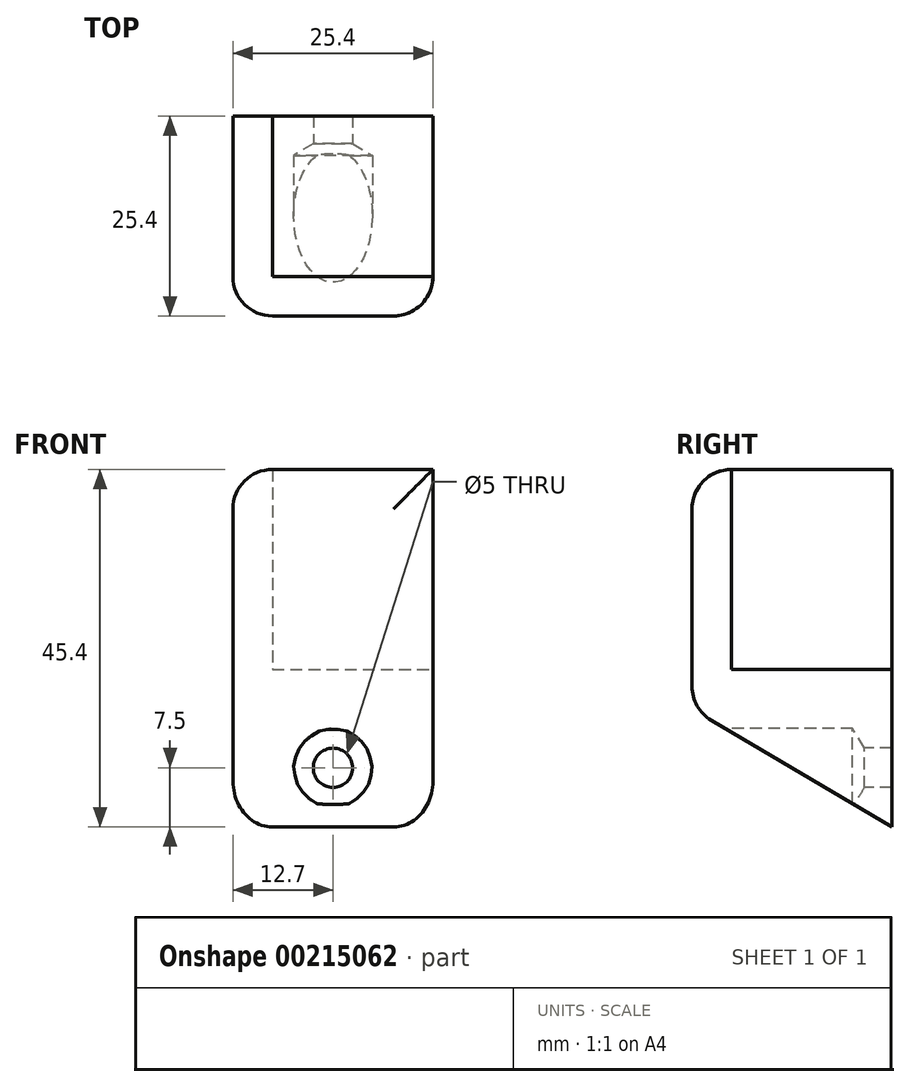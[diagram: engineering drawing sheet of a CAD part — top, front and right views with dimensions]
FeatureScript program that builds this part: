
annotation { "Feature Type Name" : "Feature", "Feature Type Description" : "" }
export const myFeature = defineFeature(function(context is Context, id is Id, definition is map)
    precondition{}
    {
        {
            var Q0;
            Q0=qCreatedBy(makeId("Top.planeOp"),FACE);
            var sketch = newSketch(context, id + "F0", { "sketchPlane" : qUnion([Q0])});
            skLineSegment(sketch, "E0.bottom", {"start": v(0, 0) * mm, "end": v(25.4, 0) * mm});
            skLineSegment(sketch, "E0.top", {"start": v(0, 25.4) * mm, "end": v(25.4, 25.4) * mm});
            skLineSegment(sketch, "E0.left", {"start": v(0, 0) * mm, "end": v(0, 25.4) * mm});
            skLineSegment(sketch, "E0.right", {"start": v(25.4, 0) * mm, "end": v(25.4, 25.4) * mm});
            skSolve(sketch);
        }
        {
            var Q0;
            Q0 = qSketchRegion(id + "F0", true);
            extrude(context, id + "F1", {"entities" : qUnion([Q0]), "depth" : 5 * mm});
        }
        {
            var Q0;
            Q0=makeQuery(id+"F1.opExtrude","CAP_FACE",FACE,{"disambiguationData":[OSD([sQuery(id+"F0.wireOp",EDGE,"E0.bottom"),sQuery(id+"F0.wireOp",EDGE,"E0.top"),sQuery(id+"F0.wireOp",EDGE,"E0.left"),sQuery(id+"F0.wireOp",EDGE,"E0.right")])],"isStart":false});
            var sketch = newSketch(context, id + "F2", { "sketchPlane" : qUnion([Q0])});
            skLineSegment(sketch, "E1", {"start": v(0, 25.4) * mm, "end": v(0, 0) * mm});
            skLineSegment(sketch, "E2", {"start": v(0, 0) * mm, "end": v(25.4, 0) * mm});
            skLineSegment(sketch, "E3", {"start": v(25.4, 0) * mm, "end": v(25.4, 5) * mm});
            skLineSegment(sketch, "E4", {"start": v(25.4, 5) * mm, "end": v(5, 5) * mm});
            skLineSegment(sketch, "E5", {"start": v(5, 5) * mm, "end": v(5, 25.4) * mm});
            skLineSegment(sketch, "E6", {"start": v(5, 25.4) * mm, "end": v(0, 25.4) * mm});
            skSolve(sketch);
        }
        {
            var Q0;
            Q0 = qSketchRegion(id + "F2", true);
            extrude(context, id + "F3", {"entities" : qUnion([Q0]), "operationType" : NewBodyOperationType.ADD, "depth" : 25.4 * mm});
        }
        {
            var Q0;
            Q0=makeQuery(id+"F3.boolean.opBoolean","MERGE",FACE,{"derivedFrom":[makeQuery(id+"F1.opExtrude","SWEPT_FACE",FACE,{"disambiguationData":[OSD([sQuery(id+"F0.wireOp",EDGE,"E0.right")])]}),makeQuery(id+"F3.opExtrude","SWEPT_FACE",FACE,{"disambiguationData":[OSD([sQuery(id+"F2.wireOp",EDGE,"E3")])]})]});
            var sketch = newSketch(context, id + "F4", { "sketchPlane" : qUnion([Q0])});
            skLineSegment(sketch, "E7", {"start": v(25.4, 0) * mm, "end": v(25.4, -15) * mm});
            skLineSegment(sketch, "E8", {"start": v(0, 0) * mm, "end": v(25.4, 0) * mm});
            skLineSegment(sketch, "E9", {"start": v(0, 0) * mm, "end": v(25.4, -15) * mm});
            skSolve(sketch);
        }
        {
            var Q0;
            Q0 = qSketchRegion(id + "F4", true);
            var Q1;
            Q1=makeQuery(id+"F3.boolean.opBoolean","MERGE",FACE,{"derivedFrom":[makeQuery(id+"F1.opExtrude","SWEPT_FACE",FACE,{"disambiguationData":[OSD([sQuery(id+"F0.wireOp",EDGE,"E0.left")])]}),makeQuery(id+"F3.opExtrude","SWEPT_FACE",FACE,{"disambiguationData":[OSD([sQuery(id+"F2.wireOp",EDGE,"E1")])]})]});
            extrude(context, id + "F5", {"entities" : qUnion([Q0]), "operationType" : NewBodyOperationType.ADD, "endBound" : BoundingType.UP_TO_SURFACE, "oppositeDirection" : true, "endBoundEntityFace" : qUnion([Q1]), "depth" : 25 * mm});
        }
        {
            var Q0;
            Q0=makeQuery(id+"F3.boolean.opBoolean","MERGE",FACE,{"derivedFrom":[makeQuery(id+"F1.opExtrude","SWEPT_FACE",FACE,{"disambiguationData":[OSD([sQuery(id+"F0.wireOp",EDGE,"E0.bottom")])]}),makeQuery(id+"F3.opExtrude","SWEPT_FACE",FACE,{"disambiguationData":[OSD([sQuery(id+"F2.wireOp",EDGE,"E2")])]})]});
            var sketch = newSketch(context, id + "F6", { "sketchPlane" : qUnion([Q0])});
            skPoint(sketch, "E10", {"position": v(12.7, -7.5) * mm});
            skSolve(sketch);
        }
        {
            var Q0;
            Q0=sQuery(id+"F6.wireOp",VERTEX,"E10");
            var Q1;
            Q1=makeQuery(id+"F1.opExtrude","SWEPT_BODY",BODY,{"disambiguationData":[OSD([sQuery(id+"F0.wireOp",EDGE,"E0.bottom"),sQuery(id+"F0.wireOp",EDGE,"E0.top"),sQuery(id+"F0.wireOp",EDGE,"E0.left"),sQuery(id+"F0.wireOp",EDGE,"E0.right")])]});
            hole(context, id + "F7", {"style" : HoleStyle.SIMPLE, "endStyle" : HoleEndStyle.THROUGH, "holeDiameter" : 5 * mm, "locations" : qUnion([Q0]), "scope" : qUnion([Q1]), "isTappedThrough" : true});
        }
        {
            var Q0;
            Q0=makeQuery(id+"F3.boolean.opBoolean","MERGE",FACE,{"derivedFrom":[makeQuery(id+"F1.opExtrude","SWEPT_FACE",FACE,{"disambiguationData":[OSD([sQuery(id+"F0.wireOp",EDGE,"E0.bottom")])]}),makeQuery(id+"F3.opExtrude","SWEPT_FACE",FACE,{"disambiguationData":[OSD([sQuery(id+"F2.wireOp",EDGE,"E2")])]})]});
            var sketch = newSketch(context, id + "F8", { "sketchPlane" : qUnion([Q0])});
            skPoint(sketch, "E11", {"position": v(12.7, -7.5) * mm});
            skSolve(sketch);
        }
        {
            var Q0;
            Q0=sQuery(id+"F8.wireOp",VERTEX,"E11");
            var Q1;
            Q1=makeQuery(id+"F1.opExtrude","SWEPT_BODY",BODY,{"disambiguationData":[OSD([sQuery(id+"F0.wireOp",EDGE,"E0.bottom"),sQuery(id+"F0.wireOp",EDGE,"E0.top"),sQuery(id+"F0.wireOp",EDGE,"E0.left"),sQuery(id+"F0.wireOp",EDGE,"E0.right")])]});
            hole(context, id + "F9", {"style" : HoleStyle.SIMPLE, "endStyle" : HoleEndStyle.BLIND, "holeDiameter" : 10 * mm, "holeDepth" : 20.4 * mm, "startFromSketch" : true, "locations" : qUnion([Q0]), "scope" : qUnion([Q1])});
        }
        {
            var Q0;
            Q0=makeQuery(id+"F3.boolean.opBoolean","MERGE",EDGE,{"derivedFrom":[makeQuery(id+"F1.opExtrude","SWEPT_EDGE",EDGE,{"disambiguationData":[OSD([sQuery(id+"F0.wireOp",EDGE,"E0.bottom"),sQuery(id+"F0.wireOp",EDGE,"E0.left")])]}),makeQuery(id+"F3.opExtrude","SWEPT_EDGE",EDGE,{"disambiguationData":[OSD([sQuery(id+"F2.wireOp",EDGE,"E1"),sQuery(id+"F2.wireOp",EDGE,"E2")])]})]});
            var Q1;
            Q1=makeQuery(id+"F5.opExtrude","CAP_EDGE",EDGE,{"disambiguationData":[OSD([sQuery(id+"F4.wireOp",EDGE,"E9")])],"isStart":false});
            var Q2;
            {var subQ0=sQuery(id+"F0.wireOp",EDGE,"E0.bottom");Q2=makeQuery(id+"F5.boolean.opBoolean","MERGE",EDGE,{"derivedFrom":[makeQuery(id+"F1.opExtrude","CAP_EDGE",EDGE,{"disambiguationData":[OSD([subQ0])],"isStart":true}),makeQuery(id+"F5.opExtrude","SWEPT_EDGE",EDGE,{"disambiguationData":[OSD([subQ0,sQuery(id+"F0.wireOp",EDGE,"E0.right"),sQuery(id+"F2.wireOp",EDGE,"E2"),sQuery(id+"F2.wireOp",EDGE,"E3"),sQuery(id+"F4.wireOp",EDGE,"E8"),sQuery(id+"F4.wireOp",EDGE,"E9")])]})]});}
            var Q3;
            Q3=makeQuery(id+"F5.opExtrude","CAP_EDGE",EDGE,{"disambiguationData":[OSD([sQuery(id+"F4.wireOp",EDGE,"E9")])],"isStart":true});
            var Q4;
            Q4=makeQuery(id+"F3.boolean.opBoolean","MERGE",EDGE,{"derivedFrom":[makeQuery(id+"F1.opExtrude","SWEPT_EDGE",EDGE,{"disambiguationData":[OSD([sQuery(id+"F0.wireOp",EDGE,"E0.bottom"),sQuery(id+"F0.wireOp",EDGE,"E0.right")])]}),makeQuery(id+"F3.opExtrude","SWEPT_EDGE",EDGE,{"disambiguationData":[OSD([sQuery(id+"F2.wireOp",EDGE,"E2"),sQuery(id+"F2.wireOp",EDGE,"E3")])]})]});
            var Q5;
            Q5=makeQuery(id+"F3.opExtrude","CAP_EDGE",EDGE,{"disambiguationData":[OSD([sQuery(id+"F2.wireOp",EDGE,"E2")])],"isStart":false});
            var Q6;
            Q6=makeQuery(id+"F3.opExtrude","CAP_EDGE",EDGE,{"disambiguationData":[OSD([sQuery(id+"F2.wireOp",EDGE,"E1")])],"isStart":false});
            fillet(context, id + "F10", {"entities" : qUnion([Q0, Q1, Q2, Q3, Q4, Q5, Q6]), "radius" : 5 * mm, "tangentPropagation" : true, "allowEdgeOverflow" : false});
        }
    });
